# Revit family: L-industry 230
name_source: partatom
category: Осветительные приборы
revit_build: Autodesk Revit 2017 (Build: 20160225_1515(x64)
units: mm (PartAtom-declared; Revit-internal decimal feet)

## family parameters
Всегда вертикально = Да
Заголовок OmniClass = Luminaries for Internal Lighting
Источник света = Да
Номер OmniClass = 23.80.70.11
Общий = Нет
Основа = Потолок
При загрузке вырезать с полостями = Нет
Размер круглого соединителя = Использовать диаметр
Тип детали = Нормальный
Точка расчета площади = Нет

## types (8) — shared parameters
Видимая форма излучения при визуализации = Нет
Длина подвеса светильника = 1008 мм
Изготовитель = LEDEL
Излучение по диаметру окружности = 136 мм
Классификация нагрузок = Освещение
Комментарии к типоразмеру = Промышленные
Описание = Светильник c аварийным блоком освещения L-office 32 Em Premium предназначен для установки в помещениях торгово-офисного и административного назначения.
Полная установленная мощность = 170 В·А
Расстояние от потолка до светильника = 1458 мм
Светофильтр = 16777215
Смещение цветовой температуры при затухании лампы = <Нет>
Угол наклона = 90.00°

## per-type parameters (varying)
| type | Артикул | Файл фотометрической сетки |
| L-industry 230 4.0К Д | 516120000741300 | L-industry 230-170-D-4.0K-01.ies |
| L-industry 230 5.0К Д | 407017 | L-industry 230-170-D-5.0K-01.ies |
| L-industry 230 4.0К К15 | 516120002741300 | L-industry 230-170-K15-4.0K-01.ies |
| L-industry 230 5.0К К15 | 407014 | L-industry 230-170-K15-5.0K-01.ies |
| L-industry 230 4.0К Г30 | 516120004741300 | L-industry 230-170-G30-4.0K-01.ies |
| L-industry 230 5.0К Г30 | 407015 | L-industry 230-170-G30-5.0K-01.ies |
| L-industry 230 4.0К Г60 | 516120006741300 | L-industry 230-170-G60-4.0K-01.ies |
| L-industry 230 5.0К Г60 | 407016 | L-industry 230-170-G60-5.0K-01.ies |

## geometry (parser evidence)
native form markers: Sweep x1
no freeform markers — native parametric forms only
